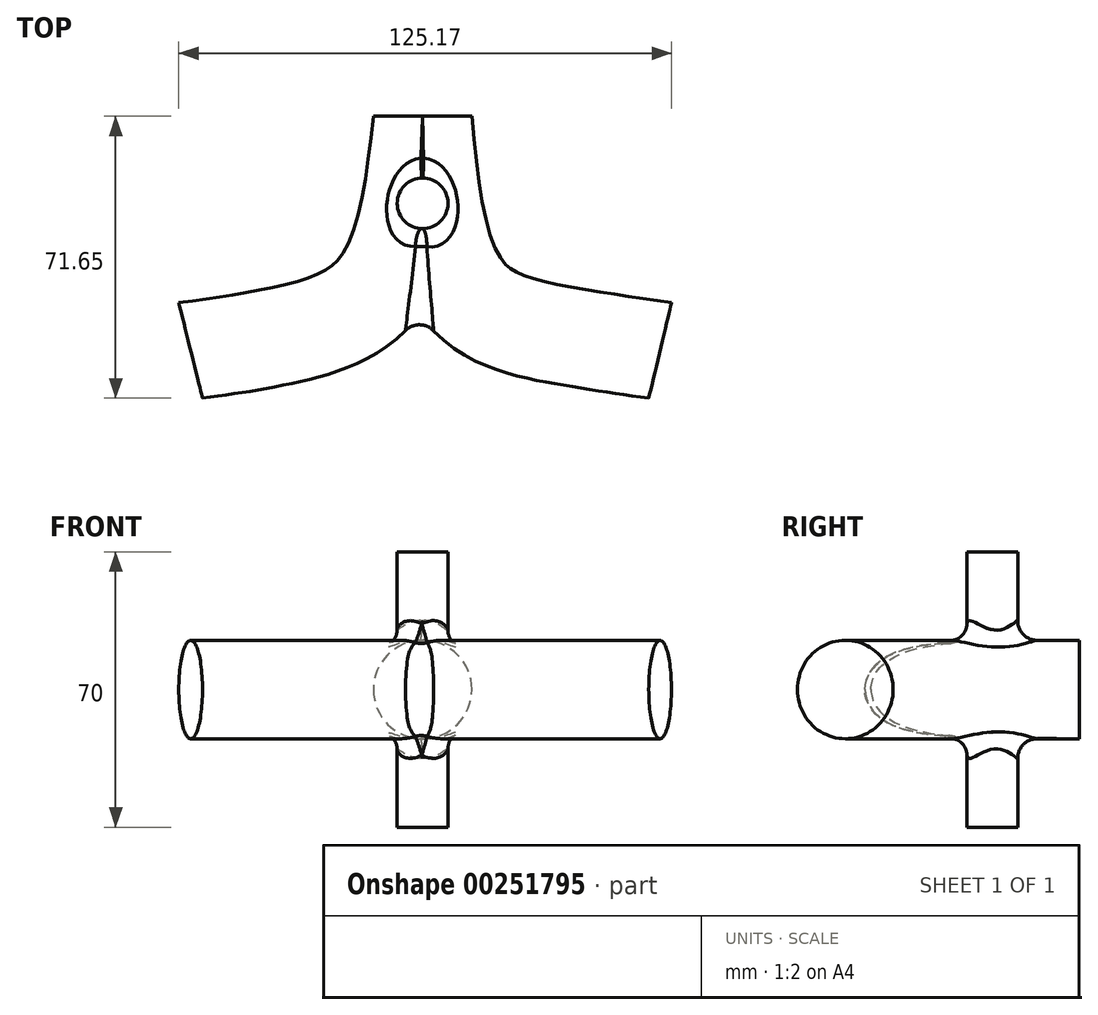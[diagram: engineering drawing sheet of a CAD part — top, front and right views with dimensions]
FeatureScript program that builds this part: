
annotation { "Feature Type Name" : "Feature", "Feature Type Description" : "" }
export const myFeature = defineFeature(function(context is Context, id is Id, definition is map)
    precondition{}
    {
        {
            var Q0;
            Q0=qCreatedBy(makeId("Front.planeOp"),FACE);
            var sketch = newSketch(context, id + "F0", { "sketchPlane" : qUnion([Q0])});
            skArc(sketch, "E0", {"start": v(12.5, 0) * mm, "mid": v(0, 12.5) * mm, "end": v(-12.5, 0) * mm});
            skLineSegment(sketch, "E1", {"start": v(-12.5, 0) * mm, "end": v(12.5, 0) * mm});
            skSolve(sketch);
        }
        {
            var Q0;
            Q0=qCreatedBy(makeId("Right.planeOp"),FACE);
            var sketch = newSketch(context, id + "F1", { "sketchPlane" : qUnion([Q0])});
            skLineSegment(sketch, "E2.bottom", {"start": v(-15.69, 0) * mm, "end": v(-22.13, 0) * mm});
            skLineSegment(sketch, "E2.top", {"start": v(-15.69, 35) * mm, "end": v(-22.13, 35) * mm});
            skLineSegment(sketch, "E2.left", {"start": v(-15.69, 0) * mm, "end": v(-15.69, 35) * mm});
            skLineSegment(sketch, "E2.right", {"start": v(-22.13, 0) * mm, "end": v(-22.13, 35) * mm});
            skPoint(sketch, "E2.middle", {"position": v(-18.9, 17.5) * mm});
            skSolve(sketch);
        }
        {
            var Q0;
            Q0 = qSketchRegion(id + "F1", true);
            var Q1;
            Q1=sQuery(id+"F1.wireOp",EDGE,"E2.right");
            revolve(context, id + "F2", {"entities" : qUnion([Q0]), "axis" : qUnion([Q1]), "revolveType" : RevolveType.FULL});
        }
        {
            var Q0;
            Q0=qCreatedBy(makeId("Top.planeOp"),FACE);
            var sketch = newSketch(context, id + "F3", { "sketchPlane" : qUnion([Q0])});
            skFitSpline(sketch, "E3", {"points": [v(0, 0) * mm, v(-11.33, -43.62) * mm, v(-34.84, -55.52) * mm, v(-58.92, -59.49) * mm], "startDerivative": vector(-14.15, -128.18) * mm, "endDerivative": vector(-80.37, -10.82) * mm});
            skFitSpline(sketch, "E4", {"points": [v(0, 0) * mm, v(11.05, -45.04) * mm, v(34.84, -55.52) * mm, v(60.34, -59.49) * mm], "startDerivative": vector(12.39, -134.12) * mm, "endDerivative": vector(83.93, -11.93) * mm});
            skSolve(sketch);
        }
        {
            var Q0;
            Q0=makeQuery(id+"F0.imprint","IMPRINT",FACE,{"disambiguationData":[TD([[makeQuery(id+"F0.imprint","IMPRINT",EDGE,{"derivedFrom":sQuery(id+"F0.wireOp",EDGE,"E0")}),1.0]])]});
            var Q1;
            Q1=sQuery(id+"F3.wireOp",EDGE,"E3");
            sweep(context, id + "F4", {"operationType" : NewBodyOperationType.ADD, "profiles" : qUnion([Q0]), "path" : qUnion([Q1])});
        }
        {
            var Q0;
            Q0=makeQuery(id+"F0.imprint","IMPRINT",FACE,{"disambiguationData":[TD([[makeQuery(id+"F0.imprint","IMPRINT",EDGE,{"derivedFrom":sQuery(id+"F0.wireOp",EDGE,"E0")}),1.0]])]});
            var Q1;
            Q1=sQuery(id+"F3.wireOp",EDGE,"E4");
            sweep(context, id + "F5", {"operationType" : NewBodyOperationType.ADD, "profiles" : qUnion([Q0]), "path" : qUnion([Q1])});
        }
        {
            var Q0;
            Q0=makeQuery(id+"F5.boolean.opBoolean","INTERSECT",EDGE,{"derivedFrom":[makeQuery(id+"F2.opRevolve","SWEPT_FACE",FACE,{"disambiguationData":[OSD([sQuery(id+"F1.wireOp",EDGE,"E2.left")])]}),makeQuery(id+"F5.opSweep","SWEPT_FACE",FACE,{"disambiguationData":[OSD([sQuery(id+"F0.wireOp",EDGE,"E0"),sQuery(id+"F3.wireOp",EDGE,"E4")])]})]});
            var Q1;
            Q1=makeQuery(id+"F4.boolean.opBoolean","INTERSECT",EDGE,{"derivedFrom":[makeQuery(id+"F2.opRevolve","SWEPT_FACE",FACE,{"disambiguationData":[OSD([sQuery(id+"F1.wireOp",EDGE,"E2.left")])]}),makeQuery(id+"F4.opSweep","SWEPT_FACE",FACE,{"disambiguationData":[OSD([sQuery(id+"F0.wireOp",EDGE,"E0"),sQuery(id+"F3.wireOp",EDGE,"E3")])]})]});
            var Q2;
            {var subQ0=sQuery(id+"F0.wireOp",EDGE,"E0");Q2=makeQuery(id+"F5.boolean.opBoolean","INTERSECT",EDGE,{"disambiguationData":[OD(1.0)],"derivedFrom":[makeQuery(id+"F4.opSweep","SWEPT_FACE",FACE,{"disambiguationData":[OSD([subQ0,sQuery(id+"F3.wireOp",EDGE,"E3")])]}),makeQuery(id+"F5.opSweep","SWEPT_FACE",FACE,{"disambiguationData":[OSD([subQ0,sQuery(id+"F3.wireOp",EDGE,"E4")])]})]});}
            fillet(context, id + "F6", {"entities" : qUnion([Q0, Q1, Q2]), "radius" : 5 * mm, "tangentPropagation" : true, "allowEdgeOverflow" : false});
        }
        {
            var Q0;
            Q0=makeQuery(id+"F2.opRevolve","SWEPT_BODY",BODY,{"disambiguationData":[OSD([sQuery(id+"F1.wireOp",EDGE,"E2.bottom"),sQuery(id+"F1.wireOp",EDGE,"E2.top"),sQuery(id+"F1.wireOp",EDGE,"E2.left"),sQuery(id+"F1.wireOp",EDGE,"E2.right")])]});
            var Q1;
            Q1=qCreatedBy(makeId("Top.planeOp"),FACE);
            mirror(context, id + "F7", {"operationType" : NewBodyOperationType.ADD, "entities" : qUnion([Q0]), "mirrorPlane" : qUnion([Q1])});
        }
    });
